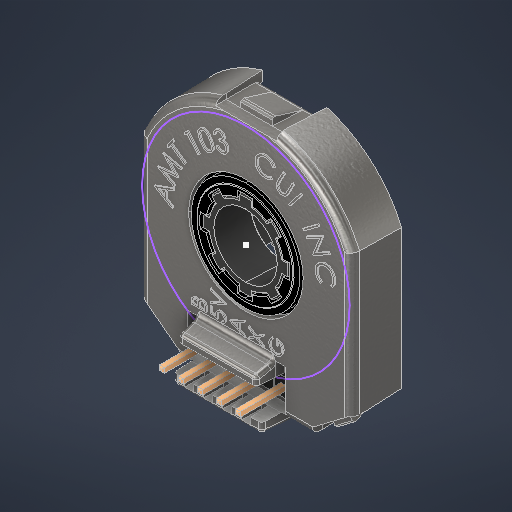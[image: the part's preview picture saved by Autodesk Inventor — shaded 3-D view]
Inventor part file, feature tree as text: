
AUTODESK INVENTOR PART (.ipt)
format: ipt  version: 2025 (Build 290162000, 162)  size: 3,852,800 bytes
history: native  units: in
note: dims shown in document units (in); Inventor stores cm internally (conversion verified against a paired STEP export)
features: other x24, sketch x1
ambient origin geometry x8: Origin, YZ Plane, XZ Plane, XY Plane, X Axis, Y Axis, Z Axis, Center Point
bodies: Solid1 (feature_tree)
feature tree (25):
  other  "amt103-v unit only.iam"
  other  "amt103-v_24.ipt:1"
  other  "amt103-v_22.ipt:1"
  other  "amt103-v_21.ipt:1"
  other  "amt103-v_20.ipt:1"
  other  "amt103-v_19.ipt:1"
  other  "amt103-v_18.ipt:1"
  other  "amt103-v_17.ipt:1"
  other  "amt103-v_16.ipt:1"
  other  "amt103-v_15.ipt:1"
  other  "amt103-v_14.ipt:1"
  other  "amt103-v_13.ipt:1"
  other  "amt103-v_12.ipt:1"
  other  "amt103-v_11.ipt:1"
  other  "amt103-v_10.ipt:1"
  other  "amt103-v_09.ipt:1"
  other  "amt103-v_08.ipt:1"
  other  "amt103-v_07.ipt:1"
  other  "amt103-v_06.ipt:1"
  other  "amt103-v_05.ipt:1"
  other  "amt103-v_04.ipt:1"
  other  "amt103-v_03.ipt:1"
  other  "amt103-v_02.ipt:1"
  other  "amt103-v_01.ipt:1"
  sketch  "Sketch1"  dims[d0=0.3937in]
